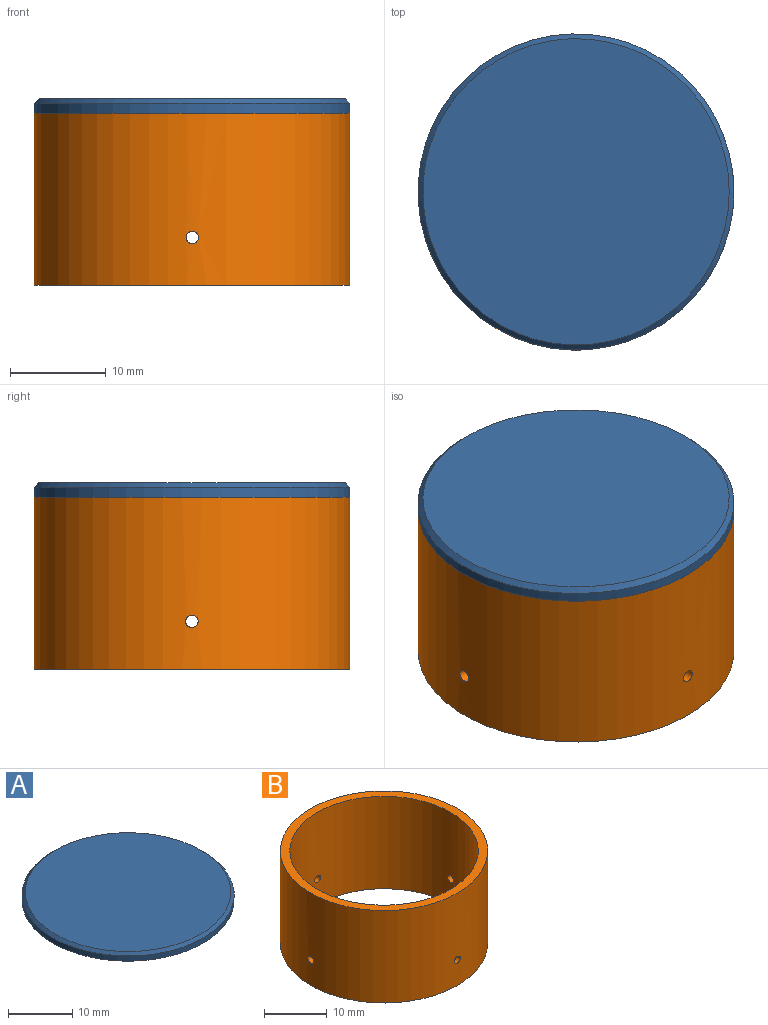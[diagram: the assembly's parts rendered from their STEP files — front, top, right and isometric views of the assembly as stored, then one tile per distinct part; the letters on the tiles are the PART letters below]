
ASSEMBLY  parts=2 mates=1
PART A: 4 faces, bbox 33x33x1.5 mm
  f0: cylinder r=16.5mm len=33mm, axis (0,0,-1), area 103.7mm2, adj f2,f3
  f1: plane 32x32mm, normal (0,0,1), area 804.2mm2, adj f3
  f2: plane 33x33mm, normal (0,0,-1), area 855.3mm2, adj f0
  f3: cone r=16mm half-angle=45deg, axis (0,0,-1), area 72.2mm2, adj f0,f1
PART B: 8 faces, bbox 33x33x18 mm
  f0: cylinder r=15mm len=30mm, axis (0,0,-1), area 1691.2mm2, adj f2,f3,f4,f5,f6,f7
  f1: cylinder r=16.5mm len=33mm, axis (0,0,-1), area 1860.8mm2, adj f2,f3,f4,f5,f6,f7
  f2: plane 33x33mm, normal (0,0,1), area 148.4mm2, adj f0,f1
  f3: plane 33x33mm, normal (0,0,-1), area 148.4mm2, adj f0,f1
  f4: cylinder r=0.65mm len=1.51mm, axis (1,0,0), area 6.1mm2, adj f0,f1
  f5: cylinder r=0.65mm len=1.51mm, axis (1,0,0), area 6.1mm2, adj f0,f1
  f6: cylinder r=0.65mm len=1.52mm, axis (0,-1,0), area 6.1mm2, adj f0,f1
  f7: cylinder r=0.65mm len=1.52mm, axis (0,-1,0), area 6.1mm2, adj f0,f1
PLACE A rot(axis=(0,1,0),0deg) t=(-54.87,110.63,-23.44)mm
PLACE B rot(axis=(0,1,0),0deg) t=(-54.87,110.63,-41.44)mm
MATE fastened B.f1 <-> A.f0  axis (0,0,1) through (-54.87,110.63,-23.44)mm
